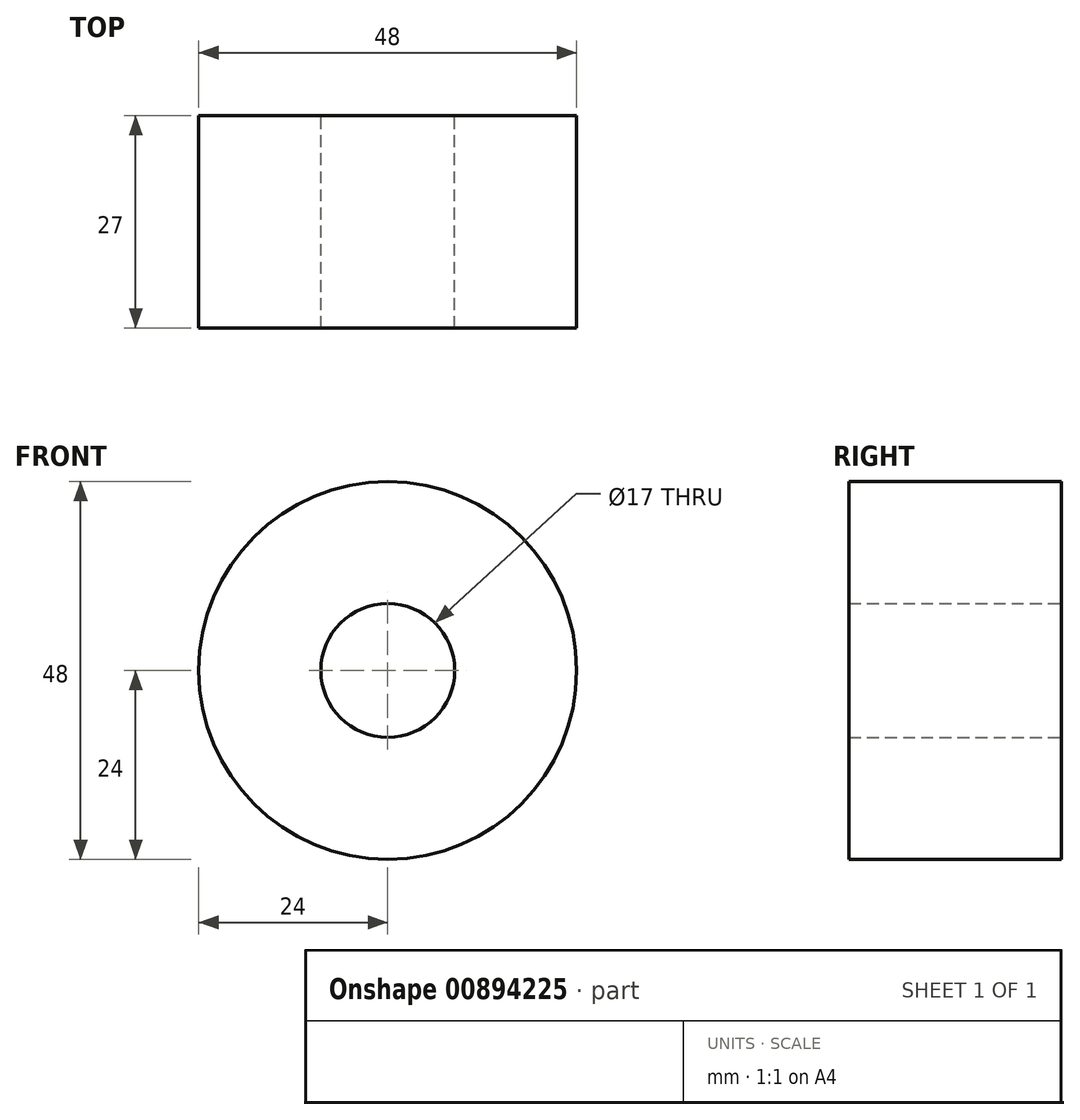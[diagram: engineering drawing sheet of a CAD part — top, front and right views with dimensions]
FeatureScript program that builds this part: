
annotation { "Feature Type Name" : "Feature", "Feature Type Description" : "" }
export const myFeature = defineFeature(function(context is Context, id is Id, definition is map)
    precondition{}
    {
        {
            var Q0;
            Q0=qCreatedBy(makeId("Front.planeOp"),FACE);
            var sketch = newSketch(context, id + "F0", { "sketchPlane" : qUnion([Q0])});
            skCircle(sketch, "E0", {"center": v(0, 0) * mm, "radius": 24 * mm});
            skCircle(sketch, "E1", {"center": v(0, 0) * mm, "radius": 8.5 * mm});
            skSolve(sketch);
        }
        {
            var Q0;
            Q0 = qSketchRegion(id + "F0", true);
            extrude(context, id + "F1", {"entities" : qUnion([Q0]), "depth" : 27 * mm, "offsetDistance" : 25 * mm});
        }
    });
